# Revit family: Drinking_Fountain-Haws_Corporation_1201S-1201SF
name_source: partatom
category: Plumbing Fixtures
revit_build: Autodesk Revit 2017 (Build: 20160225_1515(x64)
units: mm (PartAtom-declared; Revit-internal decimal feet)

## family parameters
Cut with Voids When Loaded = No
Host = Face
OmniClass Number = 23.45.05.00
Part Type = Normal
Room Calculation Point = No
Round Connector Dimension = Use Diameter
Shared = No

## types (2) — shared parameters
Assembly Code = D2010810
Default Elevation = 0' - 0"
Edition number = 1
Keynote = 15410.A1
Manufacturer = Haws Corporation
Material Bowl = Metal - Haws Corporation - Silver Powder Coated Finish
Material Bracket = Metal - Haws Corporation - Silver Powder Coated Finish
Material Bubbler = Metal - Haws Corporation - Silver Powder Coated Finish
Material Enclosure = Metal - Haws Corporation - Satin Stainless Steel
Material Plastic = Plastic - Haws Corporation - Black
Option 01 = Clearance : Forward Approach
Option 02 = Clearance : Parallel Approach
Option 03 = Clearance : Alcove Installation Forward Approach
Option 04 = Clearance : Alcove Installation Parallel Approach
Product Guid = 18b54997-3865-4947-bfd4-783f8d74b3c9
Product data url = https://bimobject.com
Tap Elevation Offset = 2' - 9"
URL = www.hawsco.com

## per-type parameters (varying)
| type | Description | Filter |
| 1201S | Single, stainless steel electric water cooler | No |
| 1201SF | Single, stainless steel, filtered electric water cooler | Yes |

note: column(s) folded — value = type name in every type: Model

## geometry (parser evidence)
native form markers: Sweep x18
no freeform markers — native parametric forms only
